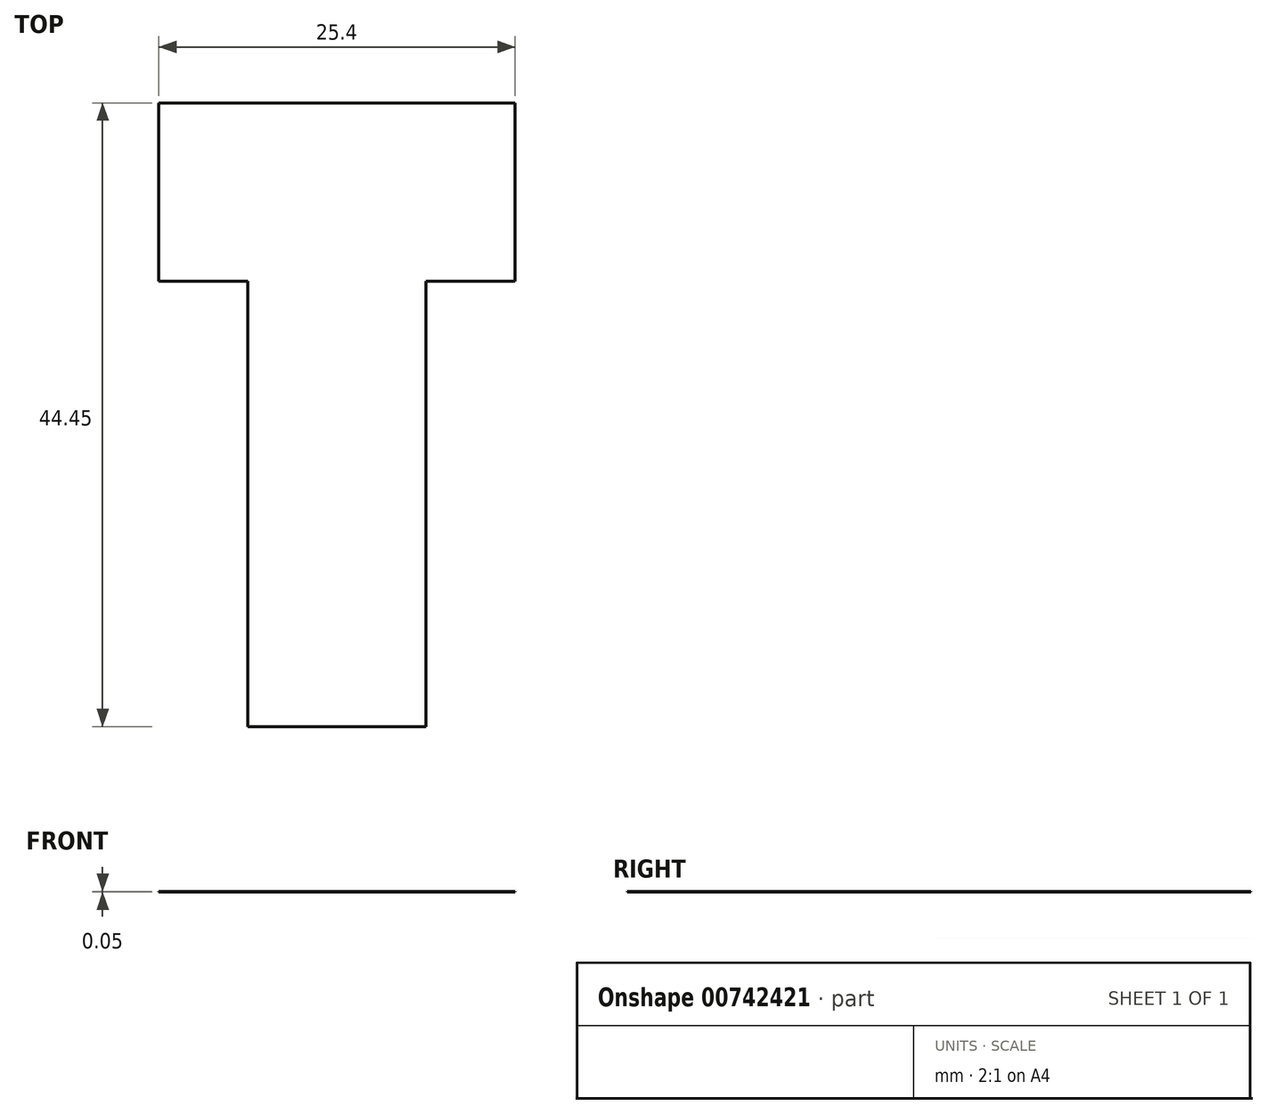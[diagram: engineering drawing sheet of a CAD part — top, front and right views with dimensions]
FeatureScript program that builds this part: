
annotation { "Feature Type Name" : "Feature", "Feature Type Description" : "" }
export const myFeature = defineFeature(function(context is Context, id is Id, definition is map)
    precondition{}
    {
        {
            var Q0;
            Q0=qCreatedBy(makeId("Top.planeOp"),FACE);
            var sketch = newSketch(context, id + "F0", { "sketchPlane" : qUnion([Q0])});
            skLineSegment(sketch, "E0", {"start": v(0, 44.45) * mm, "end": v(-13.5, 44.45) * mm});
            skLineSegment(sketch, "E1", {"start": v(-13.5, 44.45) * mm, "end": v(-13.5, 31.75) * mm});
            skLineSegment(sketch, "E2", {"start": v(-7.14, 31.75) * mm, "end": v(-13.5, 31.75) * mm});
            skLineSegment(sketch, "E3", {"start": v(-7.14, 31.75) * mm, "end": v(-7.14, 0) * mm});
            skLineSegment(sketch, "E4", {"start": v(0, 44.45) * mm, "end": v(11.9, 44.45) * mm});
            skLineSegment(sketch, "E5", {"start": v(11.9, 44.45) * mm, "end": v(11.9, 31.75) * mm});
            skLineSegment(sketch, "E6", {"start": v(11.9, 31.75) * mm, "end": v(5.56, 31.75) * mm});
            skLineSegment(sketch, "E7", {"start": v(5.56, 31.75) * mm, "end": v(5.56, 0) * mm});
            skLineSegment(sketch, "E8", {"start": v(-7.14, 0) * mm, "end": v(5.56, 0) * mm});
            skSolve(sketch);
        }
        {
            var Q0;
            Q0 = qSketchRegion(id + "F0", true);
            extrude(context, id + "F1", {"entities" : qUnion([Q0]), "depth" : 5 / 101.6 * mm, "offsetDistance" : 25.4 * mm});
        }
    });
